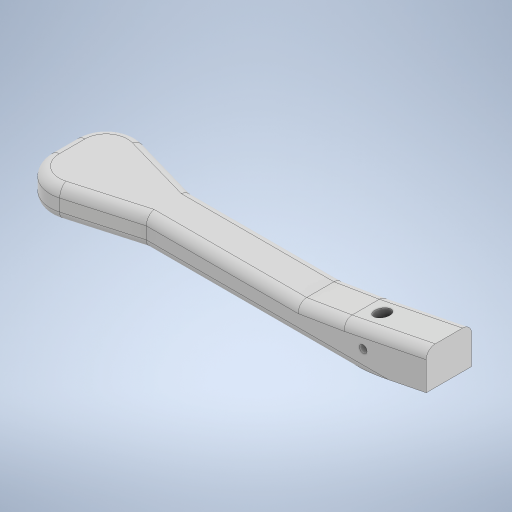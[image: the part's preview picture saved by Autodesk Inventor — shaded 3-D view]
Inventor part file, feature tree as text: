
AUTODESK INVENTOR PART (.ipt)
format: ipt  version: 2023 (Build 270158000, 158)  size: 346,112 bytes
history: native  units: mm
features: sketch x7, extrude x4, other x3, fillet x2, hole x1
ambient origin geometry x8: Origin, YZ Plane, XZ Plane, XY Plane, X Axis, Y Axis, Z Axis, Center Point
bodies: Body1 (feature_tree)
feature tree (17):
  other  "Твердое тело1"
  extrude  "Выдавливание1"  Depth=200.0mm
  fillet  "Сопряжение1"  Radius=30.0mm
  other  "РабПлоскость1"
  extrude  "Выдавливание2"  Depth=20.0mm
  sketch  "Эскиз4"
  other  "РабПлоскость2"
  sketch  "Эскиз5"
  extrude  "Выдавливание5"  Depth=20.0mm
  hole  "Отверстие1"  [1 undecoded]
  fillet  "Сопряжение5"  Radius=20.0mm
  extrude  "Выдавливание6"  Depth=20.0mm
  sketch  "Эскиз8"
  sketch  "Эскиз1"
  sketch  "Эскиз2"
  sketch  "Эскиз6"
  sketch  "Эскиз7"
note: 1 required parameter value undecoded (feature->parameter linkage not recoverable at this tier; creation-order binding heuristic only, values carry confidence <= 0.55)
